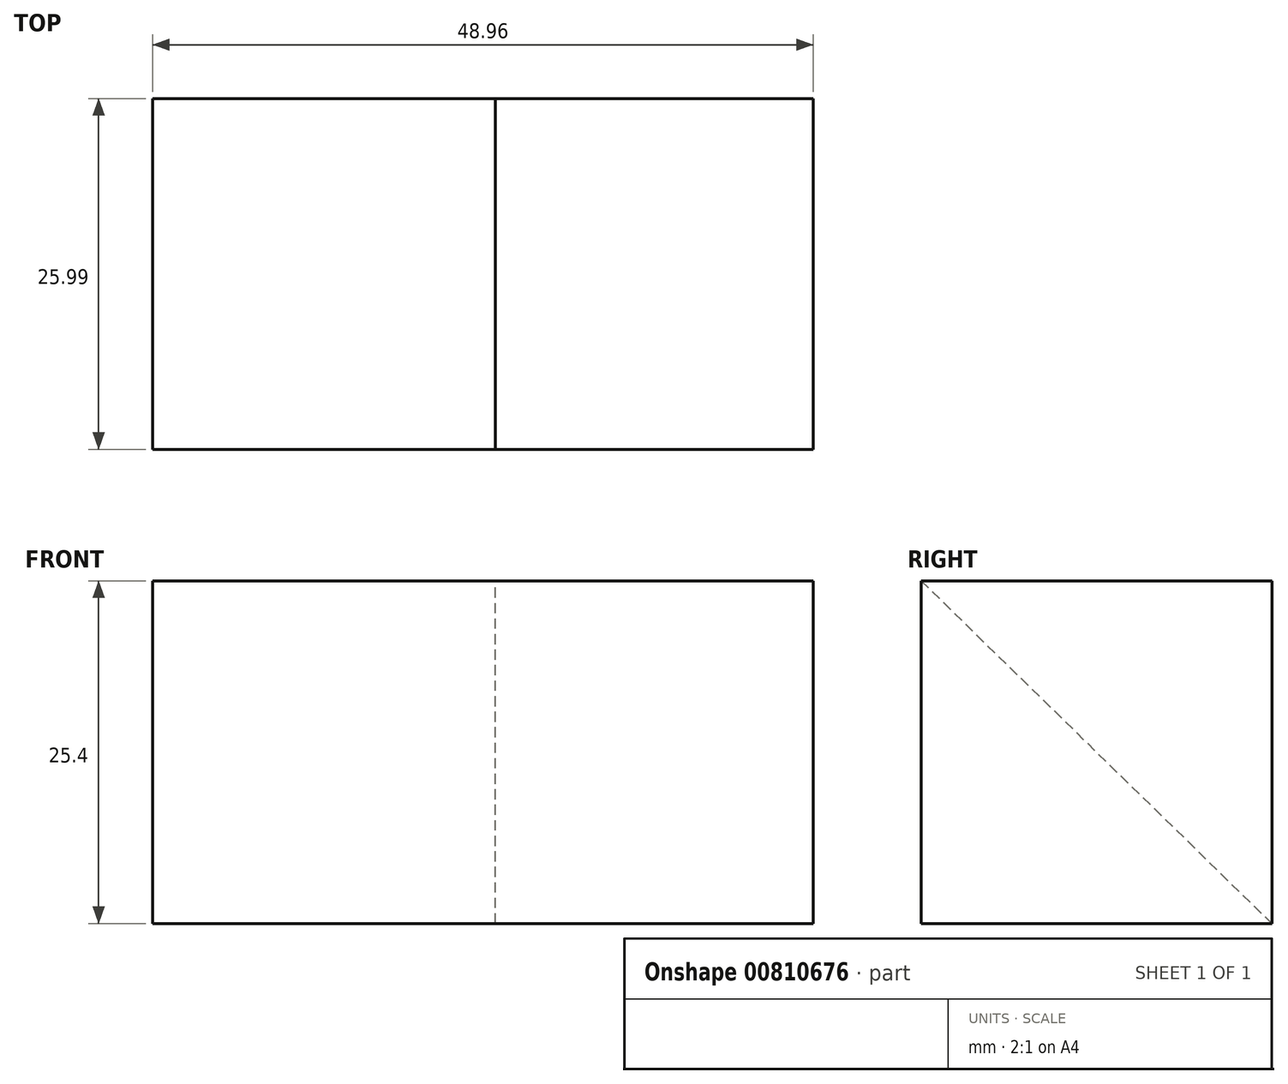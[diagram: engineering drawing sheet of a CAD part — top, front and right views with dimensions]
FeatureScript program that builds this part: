
annotation { "Feature Type Name" : "Feature", "Feature Type Description" : "" }
export const myFeature = defineFeature(function(context is Context, id is Id, definition is map)
    precondition{}
    {
        {
            var Q0;
            Q0=qCreatedBy(makeId("Top.planeOp"),FACE);
            var sketch = newSketch(context, id + "F0", { "sketchPlane" : qUnion([Q0])});
            skLineSegment(sketch, "E0.bottom", {"start": v(0, 25.99) * mm, "end": v(48.96, 25.99) * mm});
            skLineSegment(sketch, "E0.top", {"start": v(0, 0) * mm, "end": v(48.96, 0) * mm});
            skLineSegment(sketch, "E0.left", {"start": v(0, 25.99) * mm, "end": v(0, 0) * mm});
            skLineSegment(sketch, "E0.right", {"start": v(48.96, 25.99) * mm, "end": v(48.96, 0) * mm});
            skSolve(sketch);
        }
        {
            var Q0;
            Q0=makeQuery(id+"F0.imprint","IMPRINT",FACE,{"disambiguationData":[TD([[makeQuery(id+"F0.imprint","IMPRINT",EDGE,{"derivedFrom":sQuery(id+"F0.wireOp",EDGE,"E0.bottom")}),-1.0]])]});
            extrude(context, id + "F1", {"entities" : qUnion([Q0]), "oppositeDirection" : true, "depth" : 25.4 * mm, "offsetDistance" : 25.4 * mm});
        }
        {
            var Q0;
            Q0=makeQuery(id+"F1.opExtrude","SWEPT_FACE",FACE,{"disambiguationData":[OSD([sQuery(id+"F0.wireOp",EDGE,"E0.left")])]});
            var sketch = newSketch(context, id + "F2", { "sketchPlane" : qUnion([Q0])});
            skLineSegment(sketch, "E1", {"start": v(0, 0) * mm, "end": v(-25.99, -25.4) * mm});
            skSolve(sketch);
        }
        {
            var Q0;
            Q0=makeQuery(id+"F2.imprint","IMPRINT",FACE,{"disambiguationData":[TD([[makeQuery(id+"F2.imprint","IMPRINT",EDGE,{"derivedFrom":sQuery(id+"F2.wireOp",EDGE,"E1")}),-1.0]])]});
            extrude(context, id + "F3", {"entities" : qUnion([Q0]), "operationType" : NewBodyOperationType.REMOVE, "oppositeDirection" : true, "depth" : 25.4 * mm, "offsetDistance" : 25.4 * mm});
        }
    });
